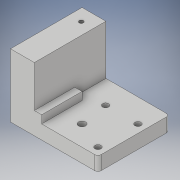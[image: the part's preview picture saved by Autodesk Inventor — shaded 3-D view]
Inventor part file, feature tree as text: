
AUTODESK INVENTOR PART (.ipt)
format: ipt  version: 2019 (Build 230136000, 136)  size: 160,256 bytes
history: native  units: in
note: dims shown in document units (in); Inventor stores cm internally (conversion verified against a paired STEP export)
features: sketch x7, extrude x4, hole x3, other x3, fillet x1, reference x1
ambient origin geometry x8: Origin, YZ Plane, XZ Plane, XY Plane, X Axis, Y Axis, Z Axis, Center Point
bodies: Solid1 (feature_tree)
feature tree (19):
  extrude  "Extrusion1"  Depth=2.1654in
  hole  "Hole1"  [1 undecoded]
  extrude  "Extrusion2"  Depth=0.5906in
  extrude  "Extrusion8"  Depth=1.2258in
  hole  "Hole2"  [1 undecoded]
  fillet  "Fillet1"  Radius=0.8in
  hole  "Hole4"  [1 undecoded]
  extrude  "Extrusion11"  Depth=0.1969in
  sketch  "Sketch1"  dims[d0=1.7717in d1=2.1654in]
  sketch  "Sketch2"  dims[d2=0.345in d3=0.0in]
  sketch  "Sketch3"  dims[d4=0.177in d5=0.2362in d6=0.332in d7=0.0787in d8=0.5635in d9=0.315in d10=0.8108in d11=0.5in]
  sketch  "Sketch9"  dims[d12=0.8937in d13=0.5906in]
  sketch  "Sketch10"  dims[d14=1.2258in d15=0.0in d40=0.315in]
  sketch  "Sketch13"  dims[d41=0.17in d42=0.0in d43=0.2in d45=0.8in]
  reference  "Reference2"
  sketch  "Sketch14"  dims[d46=0.99in d47=0.1495in d48=0.2362in d49=0.279in d50=0.0787in d51=0.5635in d52=0.315in d53=0.8108in d54=0.0787in d65=0.2in d74=0.315in d82=0.104in d83=0.276in d84=0.279in d85=0.0787in d86=0.5635in d87=0.3937in d88=0.8108in d89=1.0in d90=0.1811in d91=0.1969in d92=0.0in]
  other  "<userpath>\Documents\IQC\PolarizationMethod.iam"
  other  "PolarizationMethod.iam"
  other  "FixedFiber:1"
note: 3 required parameter values undecoded (feature->parameter linkage not recoverable at this tier; creation-order binding heuristic only, values carry confidence <= 0.55)
